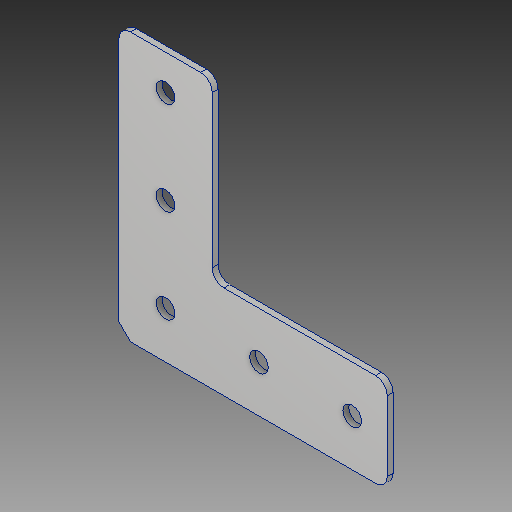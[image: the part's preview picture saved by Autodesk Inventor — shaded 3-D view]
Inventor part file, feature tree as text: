
AUTODESK INVENTOR PART (.ipt)
format: ipt  version: 2018 (Build 220112000, 112)  size: 163,328 bytes
history: native  units: in
note: dims shown in document units (in); Inventor stores cm internally (conversion verified against a paired STEP export)
features: extrude x3, sketch x3, fillet x1, chamfer x1
ambient origin geometry x8: Origin, YZ Plane, XZ Plane, XY Plane, X Axis, Y Axis, Z Axis, Center Point
bodies: Solid1 (feature_tree)
feature tree (8):
  extrude  "Extrusion1"  Depth=1.0in TaperAngle=0.0deg
  extrude  "Extrusion2"  Depth=0.125in
  extrude  "Extrusion3"  Depth=1.0in TaperAngle=0.0deg
  fillet  "Fillet2"  Radius=0.125in
  sketch  "Sketch1"  dims[d0=0.125in d1=1.0in d2=0.0in]
  sketch  "Sketch2"  dims[d4=0.0175in d5=0.0in d6=0.125in]
  sketch  "Sketch3"  dims[d7=0.125in d8=1.0in d9=0.0in d10=0.125in]
  chamfer  "Chamfer2"  [1 undecoded]
note: 1 required parameter value undecoded (feature->parameter linkage not recoverable at this tier; creation-order binding heuristic only, values carry confidence <= 0.55)
